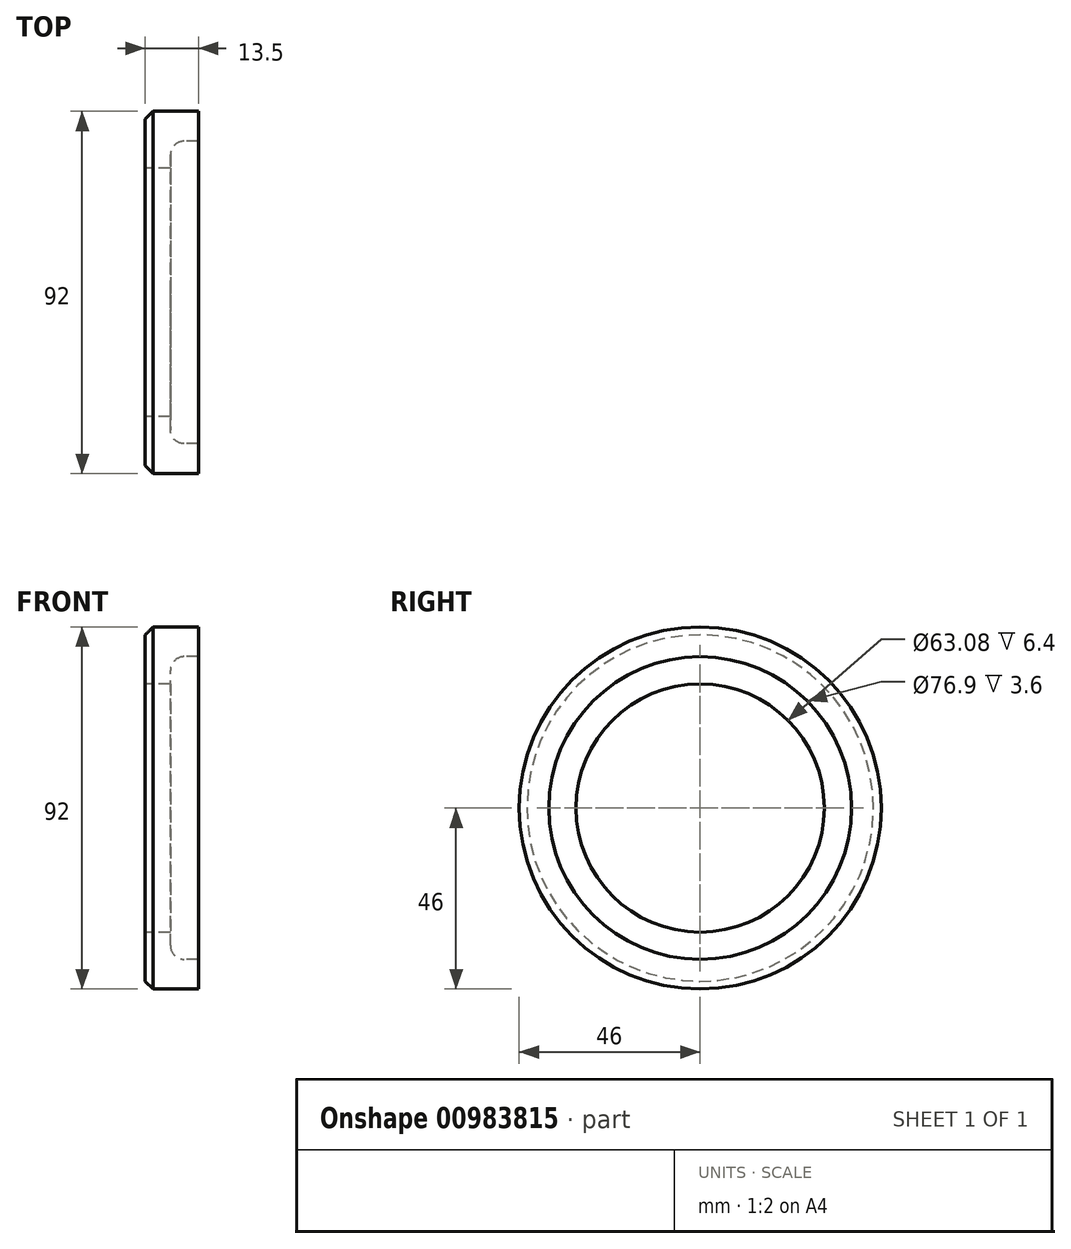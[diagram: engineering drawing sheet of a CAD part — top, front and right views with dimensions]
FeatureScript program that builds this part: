
annotation { "Feature Type Name" : "Feature", "Feature Type Description" : "" }
export const myFeature = defineFeature(function(context is Context, id is Id, definition is map)
    precondition{}
    {
        {
            var Q0;
            Q0=qCreatedBy(makeId("Front.planeOp"),FACE);
            var sketch = newSketch(context, id + "F0", { "sketchPlane" : qUnion([Q0])});
            skLineSegment(sketch, "E0", {"start": v(0, 0) * mm, "end": v(13.6, 0) * mm});
            skSolve(sketch);
        }
        {
            var Q0;
            Q0=qCreatedBy(makeId("Front.planeOp"),FACE);
            var sketch = newSketch(context, id + "F1", { "sketchPlane" : qUnion([Q0])});
            skLineSegment(sketch, "E1", {"start": v(0, 31.54) * mm, "end": v(0, 46) * mm});
            skLineSegment(sketch, "E2", {"start": v(0, 46) * mm, "end": v(13.5, 46) * mm});
            skLineSegment(sketch, "E3", {"start": v(13.5, 46) * mm, "end": v(13.5, 38.45) * mm});
            skLineSegment(sketch, "E4", {"start": v(13.5, 38.45) * mm, "end": v(9.9, 38.45) * mm});
            skLineSegment(sketch, "E5", {"start": v(0, 31.54) * mm, "end": v(6.4, 31.54) * mm});
            skLineSegment(sketch, "E6", {"start": v(6.4, 34.95) * mm, "end": v(6.4, 31.54) * mm});
            skLineSegment(sketch, "E7", {"start": v(9.9, 38.45) * mm, "end": v(6.4, 38.45) * mm});
            skLineSegment(sketch, "E8", {"start": v(6.4, 34.95) * mm, "end": v(6.4, 38.45) * mm});
            skSolve(sketch);
        }
        {
            var Q0;
            Q0=makeQuery(id+"F1.imprint","IMPRINT",FACE,{"disambiguationData":[TD([[makeQuery(id+"F1.imprint","IMPRINT",EDGE,{"derivedFrom":sQuery(id+"F1.wireOp",EDGE,"E1")}),-1.0]])]});
            var Q1;
            Q1=sQuery(id+"F0.wireOp",EDGE,"E0");
            revolve(context, id + "F2", {"surfaceOperationType" : NewSurfaceOperationType.NEW, "entities" : qUnion([Q0]), "axis" : qUnion([Q1]), "revolveType" : RevolveType.FULL});
        }
        {
            var Q0;
            Q0=makeQuery(id+"F2.opRevolve","SWEPT_EDGE",EDGE,{"disambiguationData":[OSD([sQuery(id+"F1.wireOp",EDGE,"E1"),sQuery(id+"F1.wireOp",EDGE,"E2")])]});
            chamfer(context, id + "F3", {"entities" : qUnion([Q0]), "width" : 2 * mm, "tangentPropagation" : true});
        }
        {
            var Q0;
            Q0=makeQuery(id+"F2.opRevolve","SWEPT_EDGE",EDGE,{"disambiguationData":[OSD([sQuery(id+"F1.wireOp",EDGE,"E7"),sQuery(id+"F1.wireOp",EDGE,"E8")])]});
            fillet(context, id + "F4", {"entities" : qUnion([Q0]), "radius" : 3.5 * mm, "tangentPropagation" : true, "allowEdgeOverflow" : false});
        }
    });
